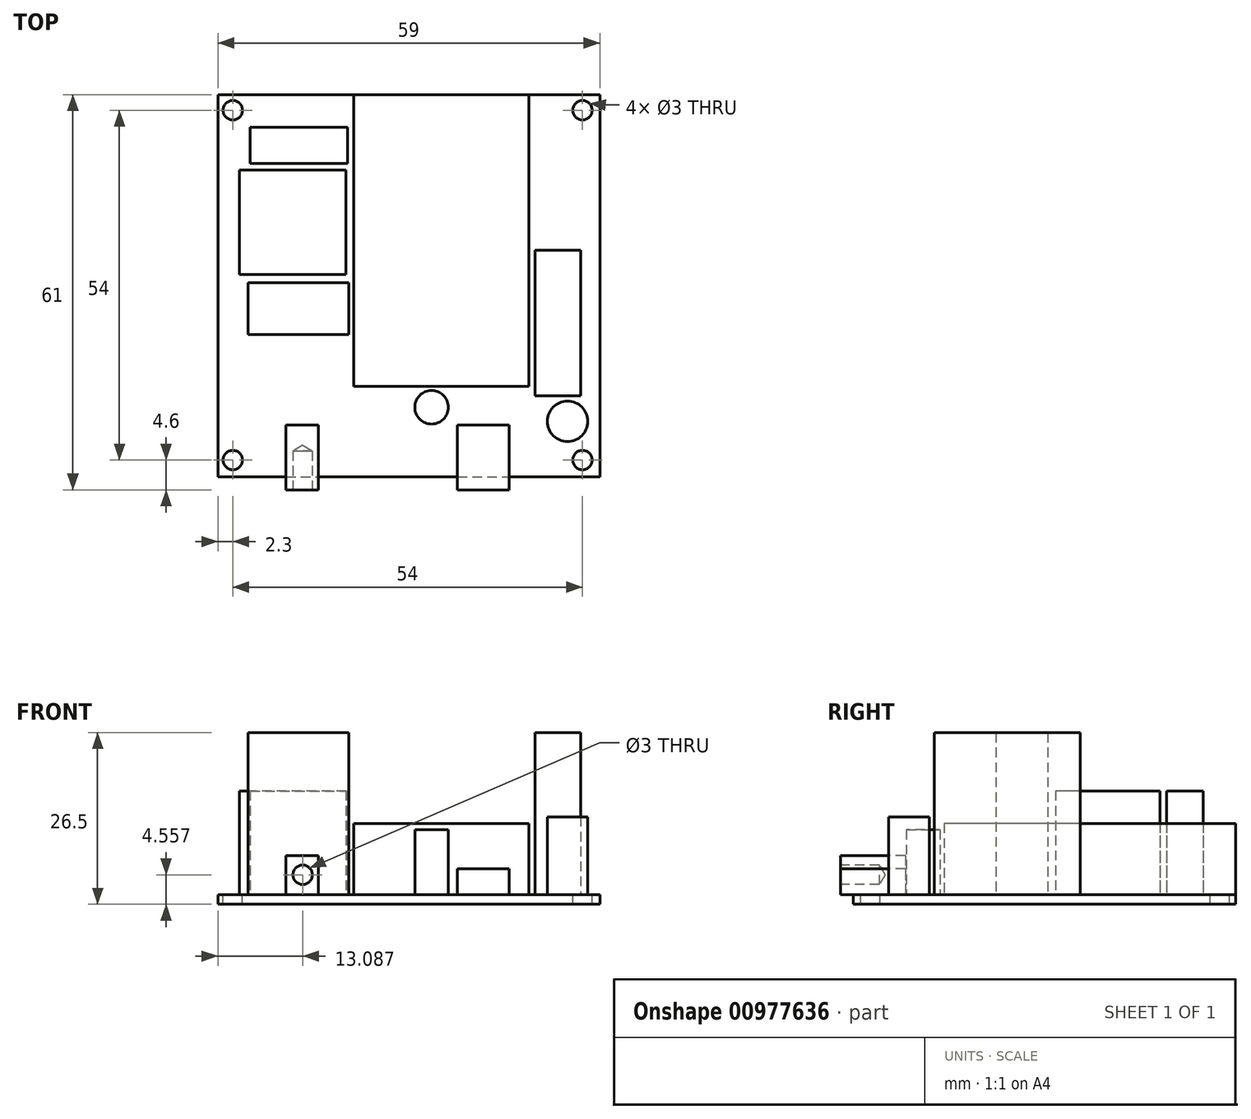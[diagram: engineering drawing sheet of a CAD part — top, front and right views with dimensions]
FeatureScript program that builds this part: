
annotation { "Feature Type Name" : "Feature", "Feature Type Description" : "" }
export const myFeature = defineFeature(function(context is Context, id is Id, definition is map)
    precondition{}
    {
        {
            var Q0;
            Q0=qCreatedBy(makeId("Top.planeOp"),FACE);
            var sketch = newSketch(context, id + "F0", { "sketchPlane" : qUnion([Q0])});
            skLineSegment(sketch, "E0.bottom", {"start": v(-29.5, 29.5) * mm, "end": v(29.5, 29.5) * mm});
            skLineSegment(sketch, "E0.top", {"start": v(-29.5, -29.5) * mm, "end": v(29.5, -29.5) * mm});
            skLineSegment(sketch, "E0.left", {"start": v(-29.5, 29.5) * mm, "end": v(-29.5, -29.5) * mm});
            skLineSegment(sketch, "E0.right", {"start": v(29.5, 29.5) * mm, "end": v(29.5, -29.5) * mm});
            skLineSegment(sketch, "E1", {"start": v(-29.5, 17.27) * mm, "end": v(0, 17.27) * mm, "construction": true});
            skLineSegment(sketch, "E2", {"start": v(0, 17.27) * mm, "end": v(29.5, 17.27) * mm, "construction": true});
            skLineSegment(sketch, "E3", {"start": v(16.95, 29.5) * mm, "end": v(16.95, 0) * mm, "construction": true});
            skLineSegment(sketch, "E4", {"start": v(16.95, 0) * mm, "end": v(16.95, -29.5) * mm, "construction": true});
            skSolve(sketch);
        }
        {
            var Q0;
            Q0=makeQuery(id+"F0.imprint","IMPRINT",FACE,{"disambiguationData":[TD([[makeQuery(id+"F0.imprint","IMPRINT",EDGE,{"derivedFrom":sQuery(id+"F0.wireOp",EDGE,"E0.bottom")}),-1.0]])]});
            extrude(context, id + "F1", {"entities" : qUnion([Q0]), "depth" : 1.5 * mm, "offsetDistance" : 25 * mm});
        }
        {
            var Q0;
            Q0=makeQuery(id+"F1.opExtrude","CAP_FACE",FACE,{"disambiguationData":[OSD([sQuery(id+"F0.wireOp",EDGE,"E0.bottom"),sQuery(id+"F0.wireOp",EDGE,"E0.top"),sQuery(id+"F0.wireOp",EDGE,"E0.left"),sQuery(id+"F0.wireOp",EDGE,"E0.right")])],"isStart":false});
            var sketch = newSketch(context, id + "F2", { "sketchPlane" : qUnion([Q0])});
            skPoint(sketch, "E5", {"position": v(26.8, -26.9) * mm});
            skPoint(sketch, "E6", {"position": v(-27.2, -26.9) * mm});
            skPoint(sketch, "E7", {"position": v(-27.2, 27.1) * mm});
            skPoint(sketch, "E8", {"position": v(26.8, 27.1) * mm});
            skLineSegment(sketch, "E9.bottom", {"start": v(-8.5, 29.5) * mm, "end": v(18.5, 29.5) * mm});
            skLineSegment(sketch, "E9.top", {"start": v(-8.5, -15.5) * mm, "end": v(18.5, -15.5) * mm});
            skLineSegment(sketch, "E9.left", {"start": v(-8.5, 29.5) * mm, "end": v(-8.5, -15.5) * mm});
            skLineSegment(sketch, "E9.right", {"start": v(18.5, 29.5) * mm, "end": v(18.5, -15.5) * mm});
            skLineSegment(sketch, "E10.bottom", {"start": v(19.5, 5.5) * mm, "end": v(26.5, 5.5) * mm});
            skLineSegment(sketch, "E10.top", {"start": v(19.5, -17) * mm, "end": v(26.5, -17) * mm});
            skLineSegment(sketch, "E10.left", {"start": v(19.5, 5.5) * mm, "end": v(19.5, -17) * mm});
            skLineSegment(sketch, "E10.right", {"start": v(26.5, 5.5) * mm, "end": v(26.5, -17) * mm});
            skLineSegment(sketch, "E11.bottom", {"start": v(-24.5, 24.5) * mm, "end": v(-9.5, 24.5) * mm});
            skLineSegment(sketch, "E11.top", {"start": v(-24.5, 18.86) * mm, "end": v(-9.5, 18.86) * mm});
            skLineSegment(sketch, "E11.left", {"start": v(-24.5, 24.5) * mm, "end": v(-24.5, 18.86) * mm});
            skLineSegment(sketch, "E11.right", {"start": v(-9.5, 24.5) * mm, "end": v(-9.5, 18.86) * mm});
            skLineSegment(sketch, "E12.bottom", {"start": v(-9.7, 17.86) * mm, "end": v(-26.2, 17.86) * mm});
            skLineSegment(sketch, "E12.top", {"start": v(-9.7, 1.72) * mm, "end": v(-26.2, 1.72) * mm});
            skLineSegment(sketch, "E12.left", {"start": v(-9.7, 17.86) * mm, "end": v(-9.7, 1.72) * mm});
            skLineSegment(sketch, "E12.right", {"start": v(-26.2, 17.86) * mm, "end": v(-26.2, 1.72) * mm});
            skLineSegment(sketch, "E13.bottom", {"start": v(-24.83, 0.5) * mm, "end": v(-9.26, 0.5) * mm});
            skLineSegment(sketch, "E13.top", {"start": v(-24.83, -7.5) * mm, "end": v(-9.26, -7.5) * mm});
            skLineSegment(sketch, "E13.left", {"start": v(-24.83, 0.5) * mm, "end": v(-24.83, -7.5) * mm});
            skLineSegment(sketch, "E13.right", {"start": v(-9.26, 0.5) * mm, "end": v(-9.26, -7.5) * mm});
            skLineSegment(sketch, "E14.bottom", {"start": v(-19, -21.5) * mm, "end": v(-14, -21.5) * mm});
            skLineSegment(sketch, "E14.top", {"start": v(-19, -29.5) * mm, "end": v(-14, -29.5) * mm});
            skLineSegment(sketch, "E14.left", {"start": v(-19, -21.5) * mm, "end": v(-19, -29.5) * mm});
            skLineSegment(sketch, "E14.right", {"start": v(-14, -21.5) * mm, "end": v(-14, -29.5) * mm});
            skLineSegment(sketch, "E15.bottom", {"start": v(7.5, -21.5) * mm, "end": v(15.5, -21.5) * mm});
            skLineSegment(sketch, "E15.top", {"start": v(7.5, -29.5) * mm, "end": v(15.5, -29.5) * mm});
            skLineSegment(sketch, "E15.left", {"start": v(7.5, -21.5) * mm, "end": v(7.5, -29.5) * mm});
            skLineSegment(sketch, "E15.right", {"start": v(15.5, -21.5) * mm, "end": v(15.5, -29.5) * mm});
            skCircle(sketch, "E16", {"center": v(24.5, -20.93) * mm, "radius": 3.13 * mm});
            skCircle(sketch, "E17", {"center": v(3.5, -18.75) * mm, "radius": 2.6 * mm});
            skLineSegment(sketch, "E18", {"start": v(-16.5, -21.5) * mm, "end": v(-16.5, -29.5) * mm, "construction": true});
            skLineSegment(sketch, "E19", {"start": v(11.5, -21.5) * mm, "end": v(11.5, -29.5) * mm, "construction": true});
            skSolve(sketch);
        }
        {
            var Q0;
            Q0=sQuery(id+"F2.wireOp",VERTEX,"E5");
            var Q1;
            Q1=sQuery(id+"F2.wireOp",VERTEX,"E6");
            var Q2;
            Q2=sQuery(id+"F2.wireOp",VERTEX,"E7");
            var Q3;
            Q3=sQuery(id+"F2.wireOp",VERTEX,"E8");
            var Q4;
            Q4=makeQuery(id+"F1.opExtrude","SWEPT_BODY",BODY,{"disambiguationData":[OSD([sQuery(id+"F0.wireOp",EDGE,"E0.bottom"),sQuery(id+"F0.wireOp",EDGE,"E0.top"),sQuery(id+"F0.wireOp",EDGE,"E0.left"),sQuery(id+"F0.wireOp",EDGE,"E0.right")])]});
            hole(context, id + "F3", {"style" : HoleStyle.SIMPLE, "endStyle" : HoleEndStyle.BLIND, "holeDiameter" : 3 * mm, "majorDiameter" : 5 * mm, "holeDepth" : 3 * mm, "isTappedThrough" : true, "tappedDepth" : 12 * mm, "tapClearance" : 3, "locations" : qUnion([Q0, Q1, Q2, Q3]), "scope" : qUnion([Q4])});
        }
        {
            var Q0;
            Q0=makeQuery(id+"F2.imprint","IMPRINT",FACE,{"disambiguationData":[TD([[makeQuery(id+"F2.imprint","IMPRINT",EDGE,{"derivedFrom":sQuery(id+"F2.wireOp",EDGE,"E9.bottom")}),-1.0]])]});
            extrude(context, id + "F4", {"entities" : qUnion([Q0]), "operationType" : NewBodyOperationType.ADD, "depth" : 11 * mm, "offsetDistance" : 25 * mm});
        }
        {
            var Q0;
            Q0=makeQuery(id+"F2.imprint","IMPRINT",FACE,{"disambiguationData":[TD([[makeQuery(id+"F2.imprint","IMPRINT",EDGE,{"derivedFrom":sQuery(id+"F2.wireOp",EDGE,"E10.bottom")}),-1.0]])]});
            extrude(context, id + "F5", {"entities" : qUnion([Q0]), "operationType" : NewBodyOperationType.ADD, "depth" : 25 * mm, "offsetDistance" : 25 * mm});
        }
        {
            var Q0;
            Q0=makeQuery(id+"F2.imprint","IMPRINT",FACE,{"disambiguationData":[TD([[makeQuery(id+"F2.imprint","IMPRINT",EDGE,{"derivedFrom":sQuery(id+"F2.wireOp",EDGE,"E11.bottom")}),-1.0]])]});
            extrude(context, id + "F6", {"entities" : qUnion([Q0]), "operationType" : NewBodyOperationType.ADD, "depth" : 16 * mm, "offsetDistance" : 25 * mm});
        }
        {
            var Q0;
            Q0=makeQuery(id+"F2.imprint","IMPRINT",FACE,{"disambiguationData":[TD([[makeQuery(id+"F2.imprint","IMPRINT",EDGE,{"derivedFrom":sQuery(id+"F2.wireOp",EDGE,"E12.bottom")}),1.0]])]});
            extrude(context, id + "F7", {"entities" : qUnion([Q0]), "operationType" : NewBodyOperationType.ADD, "depth" : 16 * mm, "offsetDistance" : 25 * mm});
        }
        {
            var Q0;
            Q0=makeQuery(id+"F2.imprint","IMPRINT",FACE,{"disambiguationData":[TD([[makeQuery(id+"F2.imprint","IMPRINT",EDGE,{"derivedFrom":sQuery(id+"F2.wireOp",EDGE,"E13.bottom")}),-1.0]])]});
            extrude(context, id + "F8", {"entities" : qUnion([Q0]), "operationType" : NewBodyOperationType.ADD, "depth" : 25 * mm, "offsetDistance" : 25 * mm});
        }
        {
            var Q0;
            {var subQ0=sQuery(id+"F2.wireOp",EDGE,"E14.top");Q0=makeQuery(id+"F2.imprint","IMPRINT",FACE,{"disambiguationData":[TD([[makeQuery(id+"F2.imprint","IMPRINT",EDGE,{"derivedFrom":subQ0}),1.0]])]});}
            var Q1;
            {var subQ0=sQuery(id+"F2.wireOp",EDGE,"E13.right");var subQ1=sQuery(id+"F2.wireOp",EDGE,"E13.top");var subQ2=makeQuery(id+"F2.imprint","INTERSECT",VERTEX,{"derivedFrom":[subQ1,subQ0]});Q1=makeQuery(id+"F2.imprint","IMPRINT",FACE,{"disambiguationData":[TD([[makeQuery(id+"F2.imprint","IMPRINT",EDGE,{"disambiguationData":[TD([[subQ2,1.0]])],"derivedFrom":subQ1}),1.0]])]});}
            extrude(context, id + "F9", {"entities" : qUnion([Q0, Q1]), "operationType" : NewBodyOperationType.ADD, "depth" : 6 * mm, "offsetDistance" : 25 * mm});
        }
        {
            var Q0;
            Q0=makeQuery(id+"F2.imprint","IMPRINT",FACE,{"disambiguationData":[TD([[makeQuery(id+"F2.imprint","IMPRINT",EDGE,{"derivedFrom":sQuery(id+"F2.wireOp",EDGE,"E16")}),1.0]])]});
            extrude(context, id + "F10", {"entities" : qUnion([Q0]), "operationType" : NewBodyOperationType.ADD, "depth" : 12 * mm, "offsetDistance" : 25 * mm});
        }
        {
            var Q0;
            Q0=makeQuery(id+"F9.boolean.opBoolean","MERGE",FACE,{"derivedFrom":[makeQuery(id+"F1.opExtrude","SWEPT_FACE",FACE,{"disambiguationData":[OSD([sQuery(id+"F0.wireOp",EDGE,"E0.top")])]}),makeQuery(id+"F9.opExtrude","SWEPT_FACE",FACE,{"disambiguationData":[OSD([sQuery(id+"F2.wireOp",EDGE,"E14.top")])]})]});
            var sketch = newSketch(context, id + "F11", { "sketchPlane" : qUnion([Q0])});
            skLineSegment(sketch, "E20.bottom", {"start": v(-19, 7.5) * mm, "end": v(-14, 7.5) * mm});
            skLineSegment(sketch, "E20.top", {"start": v(-19, 1.5) * mm, "end": v(-14, 1.5) * mm});
            skLineSegment(sketch, "E20.left", {"start": v(-19, 7.5) * mm, "end": v(-19, 1.5) * mm});
            skLineSegment(sketch, "E20.right", {"start": v(-14, 7.5) * mm, "end": v(-14, 1.5) * mm});
            skSolve(sketch);
        }
        {
            var Q0;
            Q0=makeQuery(id+"F11.imprint","IMPRINT",FACE,{"disambiguationData":[TD([[makeQuery(id+"F11.imprint","IMPRINT",EDGE,{"derivedFrom":sQuery(id+"F11.wireOp",EDGE,"E20.bottom")}),-1.0]])]});
            extrude(context, id + "F12", {"entities" : qUnion([Q0]), "operationType" : NewBodyOperationType.ADD, "depth" : 2 * mm, "offsetDistance" : 25 * mm});
        }
        {
            var Q0;
            Q0=makeQuery(id+"F12.opExtrude","CAP_FACE",FACE,{"disambiguationData":[OSD([sQuery(id+"F11.wireOp",EDGE,"E20.bottom"),sQuery(id+"F11.wireOp",EDGE,"E20.top"),sQuery(id+"F11.wireOp",EDGE,"E20.left"),sQuery(id+"F11.wireOp",EDGE,"E20.right")])],"isStart":false});
            var sketch = newSketch(context, id + "F13", { "sketchPlane" : qUnion([Q0])});
            skPoint(sketch, "E21", {"position": v(-16.41, 4.56) * mm});
            skSolve(sketch);
        }
        {
            var Q0;
            Q0=sQuery(id+"F13.wireOp",VERTEX,"E21");
            var Q1;
            Q1=makeQuery(id+"F1.opExtrude","SWEPT_BODY",BODY,{"disambiguationData":[OSD([sQuery(id+"F0.wireOp",EDGE,"E0.bottom"),sQuery(id+"F0.wireOp",EDGE,"E0.top"),sQuery(id+"F0.wireOp",EDGE,"E0.left"),sQuery(id+"F0.wireOp",EDGE,"E0.right")])]});
            hole(context, id + "F14", {"style" : HoleStyle.SIMPLE, "endStyle" : HoleEndStyle.BLIND, "holeDiameter" : 3 * mm, "majorDiameter" : 5 * mm, "holeDepth" : 6 * mm, "isTappedThrough" : true, "tappedDepth" : 12 * mm, "tapClearance" : 3, "locations" : qUnion([Q0]), "scope" : qUnion([Q1])});
        }
        {
            var Q0;
            Q0=makeQuery(id+"F2.imprint","IMPRINT",FACE,{"disambiguationData":[TD([[makeQuery(id+"F2.imprint","IMPRINT",EDGE,{"derivedFrom":sQuery(id+"F2.wireOp",EDGE,"E15.bottom")}),-1.0]])]});
            extrude(context, id + "F15", {"entities" : qUnion([Q0]), "operationType" : NewBodyOperationType.ADD, "depth" : 4 * mm, "offsetDistance" : 25 * mm});
        }
        {
            var Q0;
            Q0=makeQuery(id+"F15.boolean.opBoolean","MERGE",FACE,{"derivedFrom":[makeQuery(id+"F9.boolean.opBoolean","MERGE",FACE,{"derivedFrom":[makeQuery(id+"F1.opExtrude","SWEPT_FACE",FACE,{"disambiguationData":[OSD([sQuery(id+"F0.wireOp",EDGE,"E0.top")])]}),makeQuery(id+"F9.opExtrude","SWEPT_FACE",FACE,{"disambiguationData":[OSD([sQuery(id+"F2.wireOp",EDGE,"E14.top")])]})]}),makeQuery(id+"F15.opExtrude","SWEPT_FACE",FACE,{"disambiguationData":[OSD([sQuery(id+"F2.wireOp",EDGE,"E15.top")])]})]});
            var sketch = newSketch(context, id + "F16", { "sketchPlane" : qUnion([Q0])});
            skLineSegment(sketch, "E22.bottom", {"start": v(7.5, 5.5) * mm, "end": v(15.5, 5.5) * mm});
            skLineSegment(sketch, "E22.top", {"start": v(7.5, 1.5) * mm, "end": v(15.5, 1.5) * mm});
            skLineSegment(sketch, "E22.left", {"start": v(7.5, 5.5) * mm, "end": v(7.5, 1.5) * mm});
            skLineSegment(sketch, "E22.right", {"start": v(15.5, 5.5) * mm, "end": v(15.5, 1.5) * mm});
            skSolve(sketch);
        }
        {
            var Q0;
            Q0=makeQuery(id+"F16.imprint","IMPRINT",FACE,{"disambiguationData":[TD([[makeQuery(id+"F16.imprint","IMPRINT",EDGE,{"derivedFrom":sQuery(id+"F16.wireOp",EDGE,"E22.bottom")}),-1.0]])]});
            extrude(context, id + "F17", {"entities" : qUnion([Q0]), "operationType" : NewBodyOperationType.ADD, "depth" : 2 * mm, "offsetDistance" : 25 * mm});
        }
        {
            var Q0;
            Q0=makeQuery(id+"F2.imprint","IMPRINT",FACE,{"disambiguationData":[TD([[makeQuery(id+"F2.imprint","IMPRINT",EDGE,{"derivedFrom":sQuery(id+"F2.wireOp",EDGE,"E17")}),1.0]])]});
            extrude(context, id + "F18", {"entities" : qUnion([Q0]), "operationType" : NewBodyOperationType.ADD, "depth" : 10 * mm, "offsetDistance" : 25 * mm});
        }
    });
